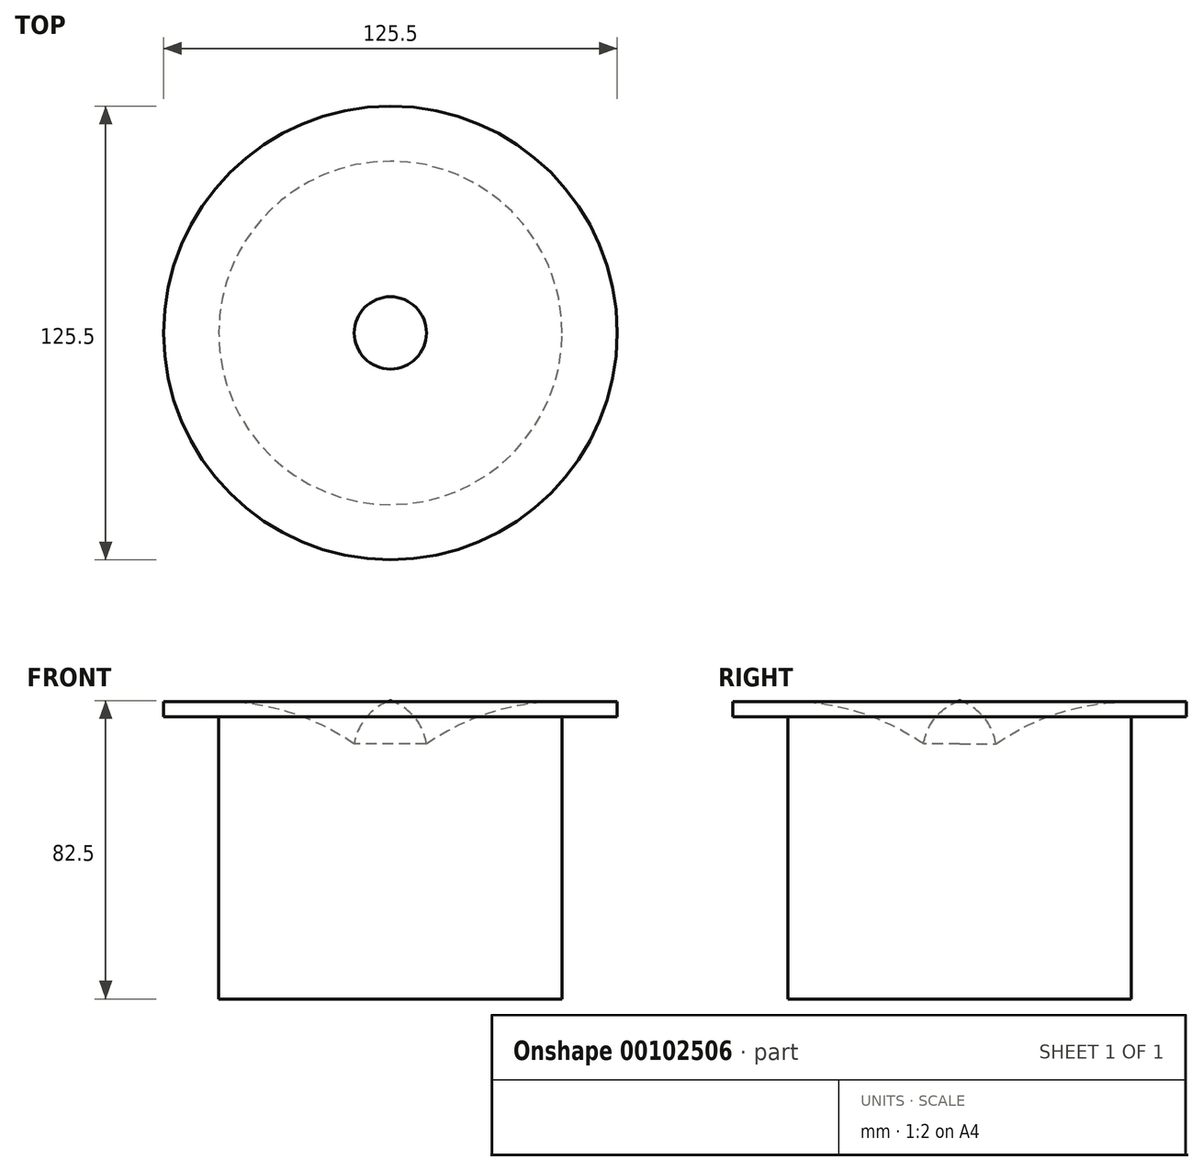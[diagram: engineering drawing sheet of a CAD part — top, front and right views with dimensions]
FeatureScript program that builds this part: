
annotation { "Feature Type Name" : "Feature", "Feature Type Description" : "" }
export const myFeature = defineFeature(function(context is Context, id is Id, definition is map)
    precondition{}
    {
        {
            var Q0;
            Q0=qCreatedBy(makeId("Front.planeOp"),FACE);
            var sketch = newSketch(context, id + "F0", { "sketchPlane" : qUnion([Q0])});
            skLineSegment(sketch, "E0", {"start": v(0, 0) * mm, "end": v(0, 82.5) * mm});
            skLineSegment(sketch, "E1", {"start": v(47.2, 82.2) * mm, "end": v(62.75, 82.2) * mm});
            skLineSegment(sketch, "E2", {"start": v(62.75, 82.2) * mm, "end": v(62.75, 78) * mm});
            skLineSegment(sketch, "E3", {"start": v(62.75, 78) * mm, "end": v(47.5, 78) * mm});
            skLineSegment(sketch, "E4", {"start": v(47.5, 78) * mm, "end": v(47.5, 0) * mm});
            skLineSegment(sketch, "E5", {"start": v(47.5, 0) * mm, "end": v(0, 0) * mm});
            skLineSegment(sketch, "E6", {"start": v(0, 0) * mm, "end": v(0, -18.23) * mm, "construction": true});
            skArc(sketch, "E7", {"start": v(10, 70.5) * mm, "mid": v(6.69, 77.9) * mm, "end": v(0, 82.5) * mm});
            skArc(sketch, "E8", {"start": v(47.2, 82.2) * mm, "mid": v(27.7, 79.2) * mm, "end": v(10, 70.5) * mm});
            skSolve(sketch);
        }
        {
            var Q0;
            Q0 = qSketchRegion(id + "F0", true);
            var Q1;
            Q1=sQuery(id+"F0.wireOp",EDGE,"E6");
            revolve(context, id + "F1", {"entities" : qUnion([Q0]), "axis" : qUnion([Q1]), "revolveType" : RevolveType.FULL});
        }
    });
